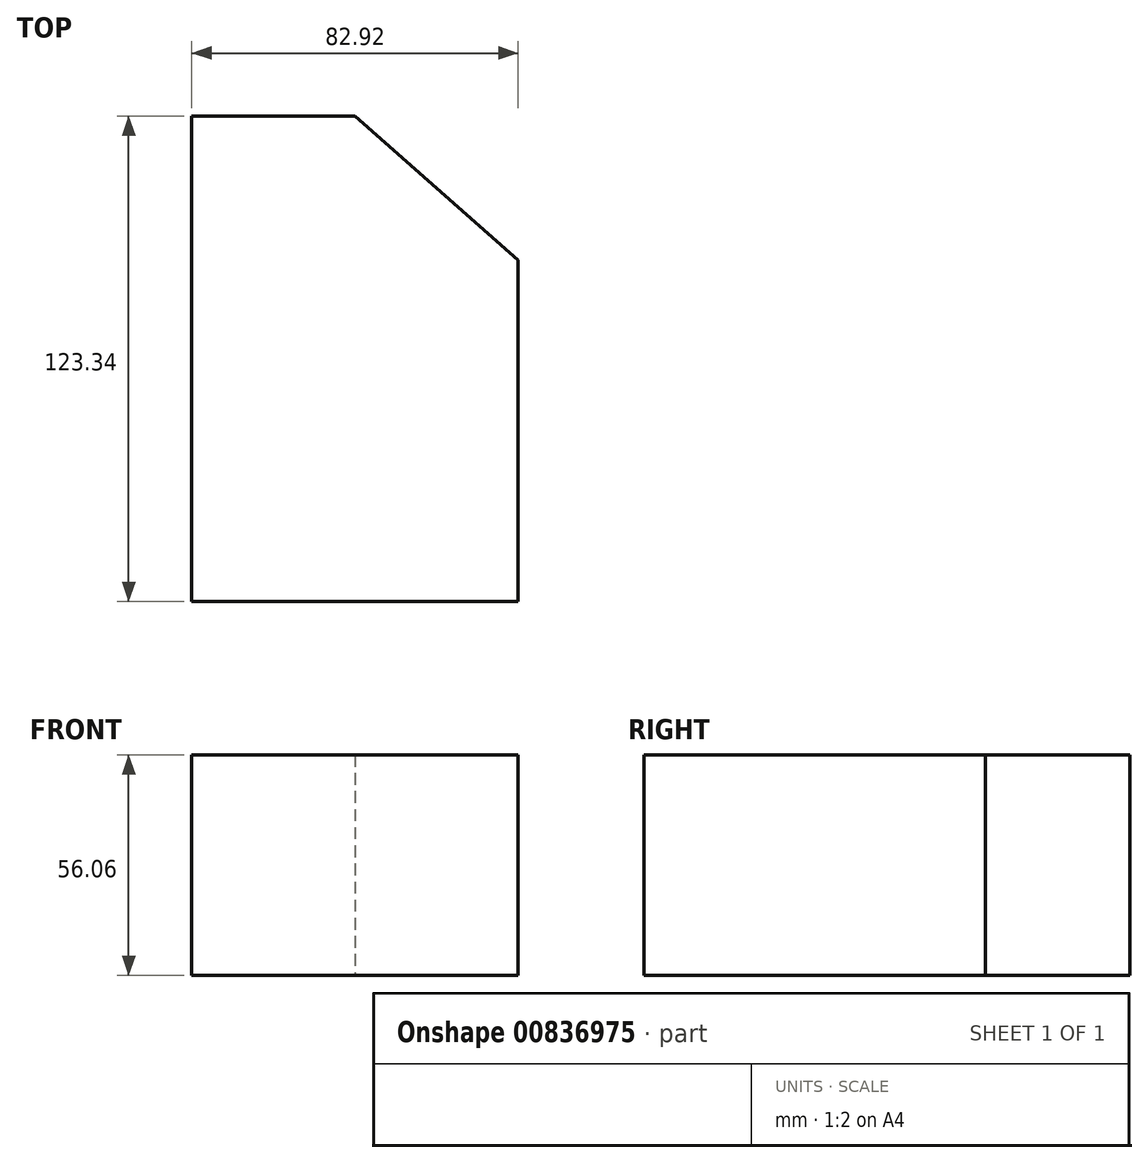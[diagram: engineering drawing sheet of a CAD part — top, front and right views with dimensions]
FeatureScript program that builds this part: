
annotation { "Feature Type Name" : "Feature", "Feature Type Description" : "" }
export const myFeature = defineFeature(function(context is Context, id is Id, definition is map)
    precondition{}
    {
        {
            var Q0;
            Q0=qCreatedBy(makeId("Top.planeOp"),FACE);
            var sketch = newSketch(context, id + "F0", { "sketchPlane" : qUnion([Q0])});
            skLineSegment(sketch, "E0.bottom", {"start": v(-35.53, 57.3) * mm, "end": v(5.93, 57.3) * mm});
            skLineSegment(sketch, "E0.top", {"start": v(-35.53, -66.04) * mm, "end": v(47.4, -66.04) * mm});
            skLineSegment(sketch, "E0.left", {"start": v(-35.53, 57.3) * mm, "end": v(-35.53, -66.04) * mm});
            skLineSegment(sketch, "E0.right", {"start": v(47.4, 20.68) * mm, "end": v(47.4, -66.04) * mm});
            skLineSegment(sketch, "E1.bottom", {"start": v(47.4, 57.3) * mm, "end": v(47.4, 57.3) * mm});
            skLineSegment(sketch, "E1.top", {"start": v(47.4, 57.3) * mm, "end": v(47.4, 57.3) * mm});
            skLineSegment(sketch, "E1.left", {"start": v(47.4, 57.3) * mm, "end": v(47.4, 57.3) * mm});
            skLineSegment(sketch, "E1.right", {"start": v(47.4, 57.3) * mm, "end": v(47.4, 57.3) * mm});
            skLineSegment(sketch, "E2", {"start": v(5.93, 57.3) * mm, "end": v(47.4, 20.68) * mm});
            skSolve(sketch);
        }
        {
            var Q0;
            Q0=makeQuery(id+"F0.imprint","IMPRINT",FACE,{"disambiguationData":[TD([[makeQuery(id+"F0.imprint","IMPRINT",EDGE,{"derivedFrom":sQuery(id+"F0.wireOp",EDGE,"E0.bottom")}),-1.0]])]});
            extrude(context, id + "F1", {"entities" : qUnion([Q0]), "depth" : 56.06 * mm, "offsetDistance" : 25.4 * mm});
        }
    });
